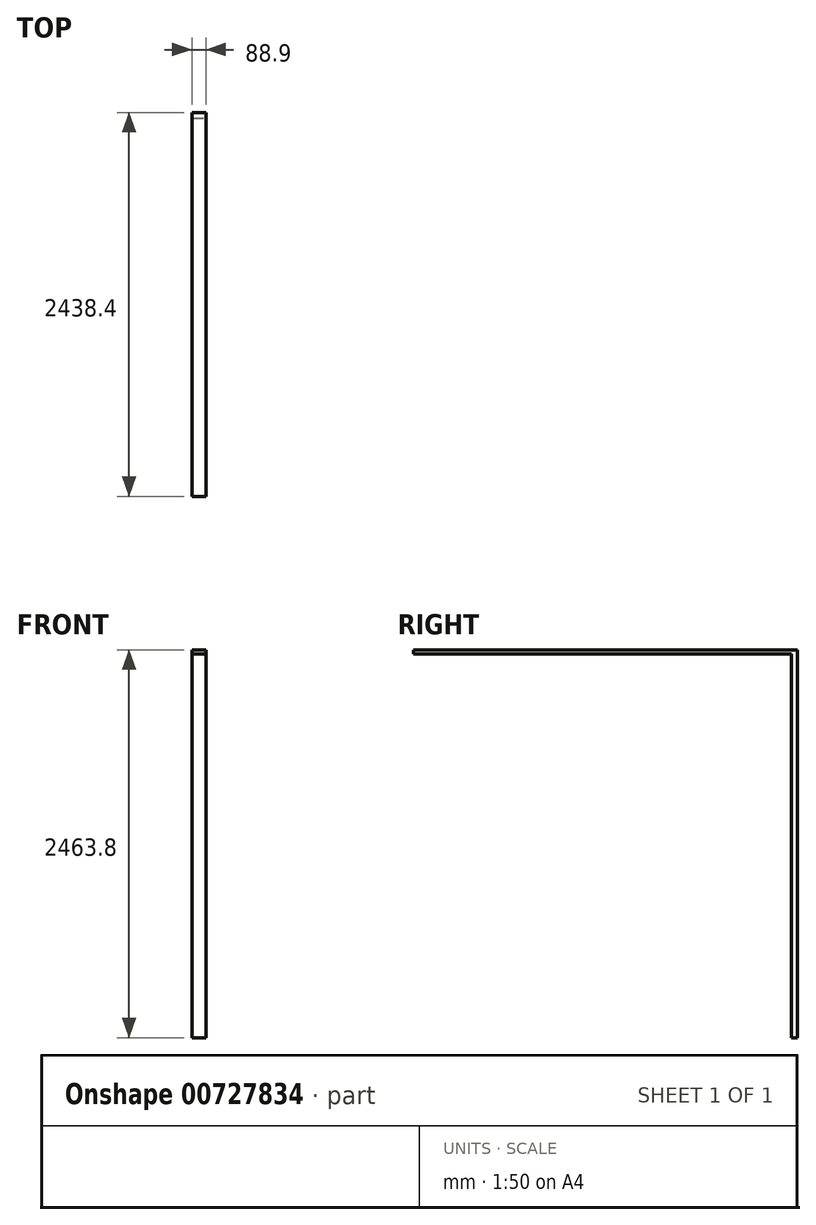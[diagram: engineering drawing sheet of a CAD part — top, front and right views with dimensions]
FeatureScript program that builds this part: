
annotation { "Feature Type Name" : "Feature", "Feature Type Description" : "" }
export const myFeature = defineFeature(function(context is Context, id is Id, definition is map)
    precondition{}
    {
        {
            var Q0;
            Q0=qCreatedBy(makeId("Front.planeOp"),FACE);
            var sketch = newSketch(context, id + "F0", { "sketchPlane" : qUnion([Q0])});
            skLineSegment(sketch, "E0.bottom", {"start": v(44.45, 12.7) * mm, "end": v(-44.45, 12.7) * mm});
            skLineSegment(sketch, "E0.top", {"start": v(44.45, -12.7) * mm, "end": v(-44.45, -12.7) * mm});
            skLineSegment(sketch, "E0.left", {"start": v(44.45, 12.7) * mm, "end": v(44.45, -12.7) * mm});
            skLineSegment(sketch, "E0.right", {"start": v(-44.45, 12.7) * mm, "end": v(-44.45, -12.7) * mm});
            skPoint(sketch, "E0.middle", {"position": v(0, 0) * mm});
            skSolve(sketch);
        }
        {
            var Q0;
            Q0 = qSketchRegion(id + "F0", true);
            extrude(context, id + "F1", {"entities" : qUnion([Q0]), "depth" : 2438.4 * mm, "offsetDistance" : 25.4 * mm});
        }
        {
            var Q0;
            Q0=makeQuery(id+"F1.opExtrude","SWEPT_FACE",FACE,{"disambiguationData":[OSD([sQuery(id+"F0.wireOp",EDGE,"E0.top")])]});
            var sketch = newSketch(context, id + "F2", { "sketchPlane" : qUnion([Q0])});
            skLineSegment(sketch, "E1", {"start": v(44.45, 0) * mm, "end": v(-44.45, 0) * mm});
            skLineSegment(sketch, "E2", {"start": v(-44.45, 0) * mm, "end": v(-44.45, 37.52) * mm});
            skLineSegment(sketch, "E3", {"start": v(-44.45, 37.52) * mm, "end": v(44.45, 37.52) * mm});
            skLineSegment(sketch, "E4", {"start": v(44.45, 37.52) * mm, "end": v(44.45, 0) * mm});
            skSolve(sketch);
        }
        {
            var Q0;
            Q0 = qSketchRegion(id + "F2", true);
            extrude(context, id + "F3", {"entities" : qUnion([Q0]), "operationType" : NewBodyOperationType.ADD, "depth" : 2438.4 * mm, "offsetDistance" : 25.4 * mm});
        }
    });
